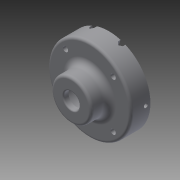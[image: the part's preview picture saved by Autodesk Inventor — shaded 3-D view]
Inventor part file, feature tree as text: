
AUTODESK INVENTOR PART (.ipt)
format: ipt  version: 2014 SP2 (Build 180246200, 246)  size: 300,032 bytes
history: native  units: mm
features: extrude x10, sketch x10, fillet x4, chamfer x1
ambient origin geometry x8: Origin, YZ Plane, XZ Plane, XY Plane, X Axis, Y Axis, Z Axis, Center Point
bodies: Solid1 (feature_tree)
feature tree (25):
  extrude  "Extrusion1"  Depth=31.0mm
  extrude  "Extrusion2"  Depth=4.0mm
  extrude  "Extrusion3"  Depth=10.0mm
  extrude  "Extrusion4"  Depth=15.0mm TaperAngle=0.0deg
  extrude  "Extrusion5"  Depth=6.0mm
  extrude  "Extrusion6"  Depth=27.0mm
  extrude  "Extrusion7"  Depth=7.0mm
  extrude  "Extrusion8"  Depth=16.0mm
  extrude  "Extrusion9"  Depth=7.0mm
  fillet  "Fillet1"  Radius=3.5mm
  fillet  "Fillet2"  Radius=16.0mm
  fillet  "Fillet3"  Radius=9.0mm
  fillet  "Fillet4"  Radius=2.0mm
  extrude  "Extrusion10"  Depth=2.0mm
  chamfer  "Chamfer1"  Distance=7.0mm
  sketch  "Sketch1"  dims[d0=12.0mm d1=31.0mm]
  sketch  "Sketch2"  dims[d2=4.0mm d3=0.0mm d4=23.0mm]
  sketch  "Sketch3"  dims[d5=10.0mm d6=0.0mm d8=26.0mm]
  sketch  "Sketch4"  dims[d9=64.0mm d10=15.0mm d11=0.0mm]
  sketch  "Sketch5"  dims[d12=6.0mm d13=3.0mm]
  sketch  "Sketch6"  dims[d14=54.0mm d15=27.0mm]
  sketch  "Sketch7"  dims[d16=13.0mm d17=7.0mm]
  sketch  "Sketch8"  dims[d18=3.5mm d19=16.0mm]
  sketch  "Sketch9"  dims[d20=13.0mm d21=7.0mm d22=3.5mm d23=16.0mm d24=9.0mm d25=0.0mm d26=2.0mm d27=0.0mm]
  sketch  "Sketch10"  dims[d28=2.0mm d29=0.0mm d30=3.0mm d31=7.0mm d32=3.5mm d33=3.5mm d34=3.0mm d35=0.0mm d36=3.0mm d37=3.5mm d39=3.5mm d40=3.0mm d41=0.0mm d42=52.0mm d43=4.0mm d44=4.0mm d45=4.0mm d46=4.0mm d47=25.0mm d48=0.0mm d49=2.0mm d50=5.0mm d51=2.0mm d52=1.0mm d53=2.0mm d54=82.201441mm d55=29.918878mm d56=2.0mm d57=2.0mm d58=2.0mm d59=4.0mm d60=0.0mm d61=2.0mm d62=2.0mm d63=45.0deg]
